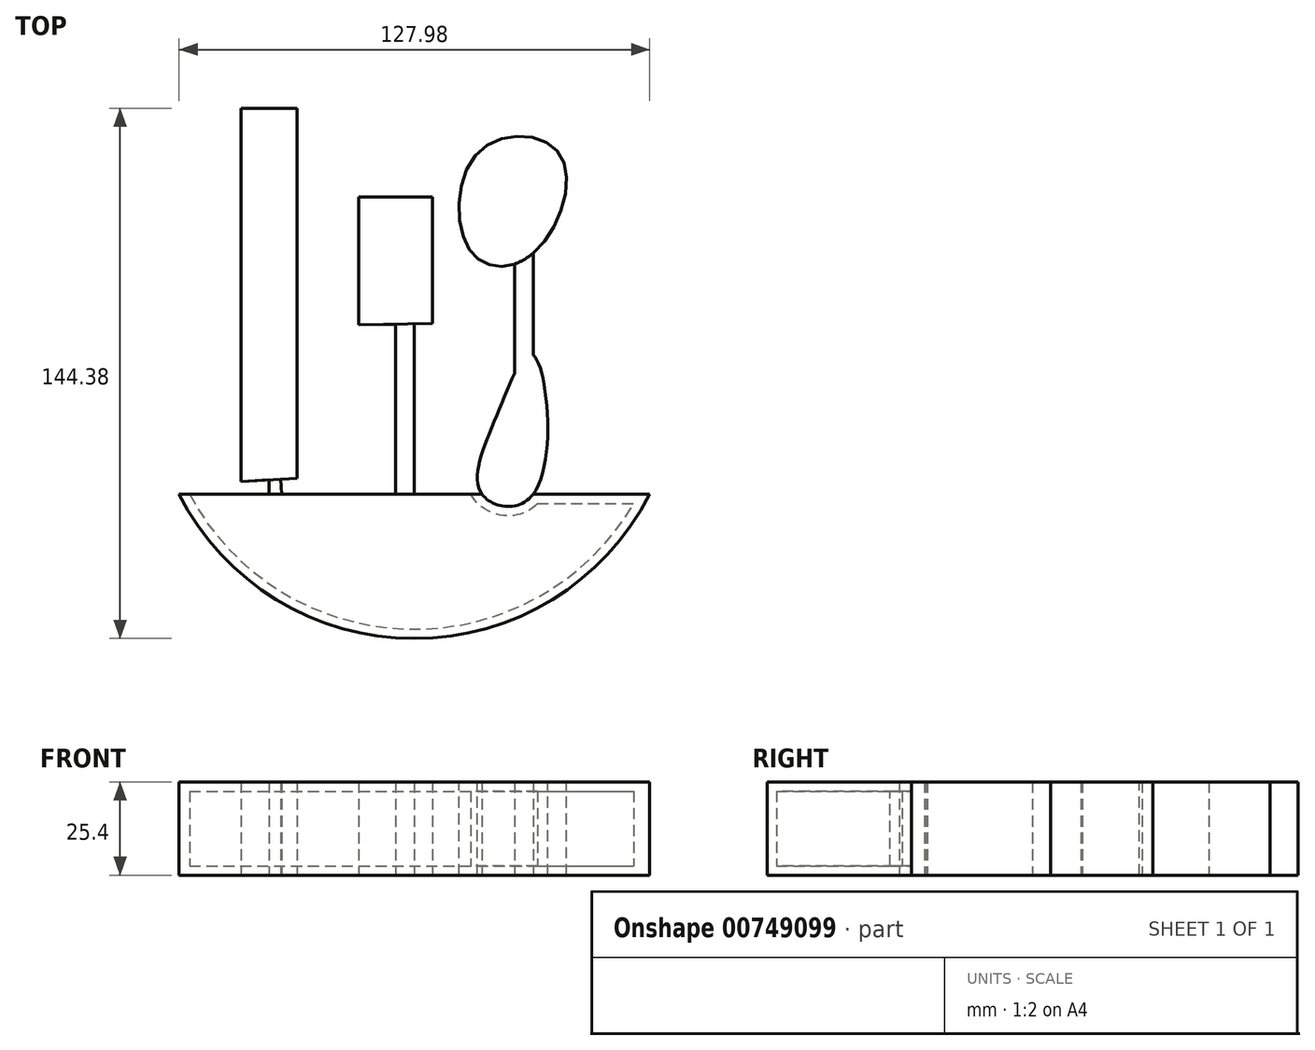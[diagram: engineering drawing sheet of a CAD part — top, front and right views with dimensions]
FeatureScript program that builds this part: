
annotation { "Feature Type Name" : "Feature", "Feature Type Description" : "" }
export const myFeature = defineFeature(function(context is Context, id is Id, definition is map)
    precondition{}
    {
        {
            var Q0;
            Q0=qCreatedBy(makeId("Top.planeOp"),FACE);
            var sketch = newSketch(context, id + "F0", { "sketchPlane" : qUnion([Q0])});
            skLineSegment(sketch, "E0", {"start": v(-52.17, -52.17) * mm, "end": v(-52.17, 49.43) * mm});
            skLineSegment(sketch, "E1", {"start": v(-52.17, 49.43) * mm, "end": v(-36.93, 49.43) * mm});
            skLineSegment(sketch, "E2", {"start": v(-36.93, 49.43) * mm, "end": v(-36.93, -51.39) * mm});
            skLineSegment(sketch, "E3", {"start": v(-20.12, -9.57) * mm, "end": v(-20.12, 25.2) * mm});
            skLineSegment(sketch, "E4", {"start": v(-20.12, 25.2) * mm, "end": v(0, 25.2) * mm});
            skLineSegment(sketch, "E5", {"start": v(0, 25.2) * mm, "end": v(0, -9.18) * mm});
            skLineSegment(sketch, "E6", {"start": v(0, -9.18) * mm, "end": v(-20.12, -9.57) * mm});
            skLineSegment(sketch, "E7", {"start": v(-36.93, -51.39) * mm, "end": v(-52.17, -52.17) * mm});
            skLineSegment(sketch, "E8", {"start": v(-10.06, -9.38) * mm, "end": v(-10.06, -55.68) * mm});
            skLineSegment(sketch, "E9", {"start": v(-10.06, -55.68) * mm, "end": v(59, -55.68) * mm});
            skLineSegment(sketch, "E10", {"start": v(59, -55.68) * mm, "end": v(-68.97, -55.68) * mm});
            skArc(sketch, "E11", {"start": v(-68.97, -55.68) * mm, "mid": v(-4.98, -94.95) * mm, "end": v(59, -55.68) * mm});
            skLineSegment(sketch, "E12", {"start": v(-44.55, -51.78) * mm, "end": v(-44.55, -55.68) * mm});
            skLineSegment(sketch, "E13", {"start": v(27.35, -17.78) * mm, "end": v(27.35, 9.96) * mm});
            skFitSpline(sketch, "E14", {"points": [v(13.48, -55.68) * mm, v(17.78, -33.41) * mm, v(27.35, -17.78) * mm, v(27.35, -55.68) * mm, v(13.48, -55.68) * mm]});
            skFitSpline(sketch, "E15", {"points": [v(27.35, 9.96) * mm, v(10.75, 9.96) * mm, v(12.7, 37.7) * mm, v(34.58, 36.93) * mm, v(27.35, 9.96) * mm]});
            skLineSegment(sketch, "E16", {"start": v(-4.98, -55.68) * mm, "end": v(-4.98, -9.28) * mm});
            skLineSegment(sketch, "E17", {"start": v(-41.27, -51.6) * mm, "end": v(-41.07, -55.68) * mm});
            skLineSegment(sketch, "E18", {"start": v(22.27, -22.8) * mm, "end": v(22.27, 7.01) * mm});
            skSolve(sketch);
        }
        {
            var Q0;
            {var subQ0=sQuery(id+"F0.wireOp",EDGE,"E11");Q0=makeQuery(id+"F0.imprint","IMPRINT",FACE,{"disambiguationData":[TD([[makeQuery(id+"F0.imprint","IMPRINT",EDGE,{"derivedFrom":subQ0}),1.0]])]});}
            var Q1;
            {var subQ3=sQuery(id+"F0.wireOp",EDGE,"E0");Q1=makeQuery(id+"F0.imprint","IMPRINT",FACE,{"disambiguationData":[TD([[makeQuery(id+"F0.imprint","IMPRINT",EDGE,{"derivedFrom":subQ3}),-1.0]])]});}
            var Q2;
            {var subQ3=sQuery(id+"F0.wireOp",EDGE,"E3");Q2=makeQuery(id+"F0.imprint","IMPRINT",FACE,{"disambiguationData":[TD([[makeQuery(id+"F0.imprint","IMPRINT",EDGE,{"derivedFrom":subQ3}),-1.0]])]});}
            var Q3;
            {var subQ0=sQuery(id+"F0.wireOp",EDGE,"E14");var subQ4=makeQuery(id+"F0.imprint","IMPRINT",VERTEX,{"derivedFrom":subQ0});Q3=makeQuery(id+"F0.imprint","IMPRINT",FACE,{"disambiguationData":[TD([[makeQuery(id+"F0.imprint","IMPRINT",EDGE,{"disambiguationData":[TD([[subQ4,1.0]])],"derivedFrom":subQ0}),-1.0]])]});}
            var Q4;
            Q4=makeQuery(id+"F0.imprint","IMPRINT",FACE,{"disambiguationData":[TD([[makeQuery(id+"F0.imprint","IMPRINT",EDGE,{"derivedFrom":sQuery(id+"F0.wireOp",EDGE,"E15")}),-1.0]])]});
            var Q5;
            {var subQ0=sQuery(id+"F0.wireOp",EDGE,"E14");var subQ1=sQuery(id+"F0.wireOp",EDGE,"E10");var subQ2=makeQuery(id+"F0.imprint","INTERSECT",VERTEX,{"disambiguationData":[OD(0.0)],"derivedFrom":[subQ1,subQ0]});Q5=makeQuery(id+"F0.imprint","IMPRINT",FACE,{"disambiguationData":[TD([[makeQuery(id+"F0.imprint","IMPRINT",EDGE,{"disambiguationData":[TD([[subQ2,-1.0]])],"derivedFrom":subQ1}),1.0]])]});}
            extrude(context, id + "F1", {"entities" : qUnion([Q0, Q1, Q2, Q3, Q4, Q5]), "depth" : 25.4 * mm, "offsetDistance" : 25.4 * mm});
        }
        {
            var Q0;
            Q0 = qSketchRegion(id + "F0", true);
            extrude(context, id + "F2", {"entities" : qUnion([Q0]), "depth" : 25.4 * mm, "offsetDistance" : 25.4 * mm});
        }
        {
            var Q0;
            Q0=makeQuery(id+"F1.opExtrude","SWEPT_FACE",FACE,{"disambiguationData":[OSD([sQuery(id+"F0.wireOp",EDGE,"E10")])]});
            shell(context, id + "F3", {"entities" : qUnion([Q0]), "thickness" : 2.54 * mm});
        }
    });
